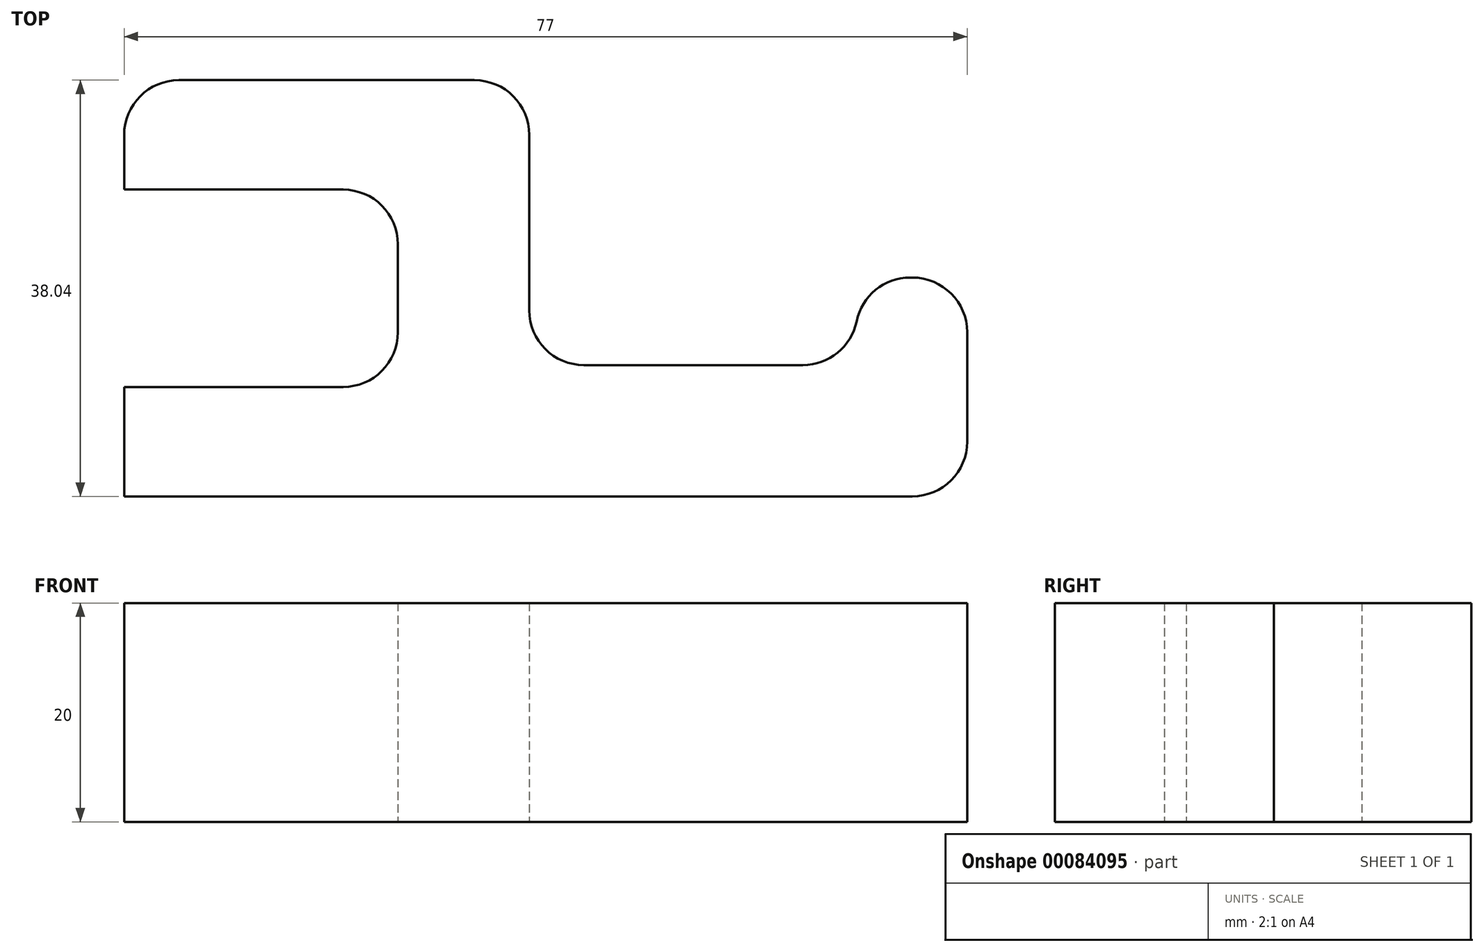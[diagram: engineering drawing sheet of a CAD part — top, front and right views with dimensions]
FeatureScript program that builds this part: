
annotation { "Feature Type Name" : "Feature", "Feature Type Description" : "" }
export const myFeature = defineFeature(function(context is Context, id is Id, definition is map)
    precondition{}
    {
        {
            var Q0;
            Q0=qCreatedBy(makeId("Front.planeOp"),FACE);
            var sketch = newSketch(context, id + "F0", { "sketchPlane" : qUnion([Q0])});
            skLineSegment(sketch, "E0", {"start": v(5, 38.04) * mm, "end": v(32, 38.04) * mm});
            skLineSegment(sketch, "E1", {"start": v(37, 33.04) * mm, "end": v(37, 17) * mm});
            skLineSegment(sketch, "E2", {"start": v(42, 12) * mm, "end": v(62, 12) * mm});
            skLineSegment(sketch, "E3", {"start": v(67, 17) * mm, "end": v(67, 20) * mm});
            skLineSegment(sketch, "E4", {"start": v(67, 20) * mm, "end": v(77, 20) * mm});
            skLineSegment(sketch, "E5", {"start": v(77, 20) * mm, "end": v(77, 5) * mm});
            skLineSegment(sketch, "E6", {"start": v(72, 0) * mm, "end": v(0, 0) * mm});
            skPoint(sketch, "E7.visualSharp", {"position": v(37, 12) * mm});
            skArc(sketch, "E7.filletArc", {"start": v(37, 17) * mm, "mid": v(38.46, 13.46) * mm, "end": v(42, 12) * mm});
            skPoint(sketch, "E8.visualSharp", {"position": v(67, 12) * mm});
            skArc(sketch, "E8.filletArc", {"start": v(62, 12) * mm, "mid": v(65.54, 13.46) * mm, "end": v(67, 17) * mm});
            skPoint(sketch, "E9.visualSharp", {"position": v(77, 0) * mm});
            skArc(sketch, "E9.filletArc", {"start": v(72, 0) * mm, "mid": v(75.54, 1.46) * mm, "end": v(77, 5) * mm});
            skLineSegment(sketch, "E10", {"start": v(0, 28.04) * mm, "end": v(20, 28.04) * mm});
            skLineSegment(sketch, "E11", {"start": v(25, 23.04) * mm, "end": v(25, 15) * mm});
            skLineSegment(sketch, "E12", {"start": v(20, 10) * mm, "end": v(0, 10) * mm});
            skLineSegment(sketch, "E13", {"start": v(0, 10) * mm, "end": v(0, 0) * mm});
            skPoint(sketch, "E14.visualSharp", {"position": v(25, 10) * mm});
            skArc(sketch, "E14.filletArc", {"start": v(20, 10) * mm, "mid": v(23.54, 11.46) * mm, "end": v(25, 15) * mm});
            skPoint(sketch, "E15.visualSharp", {"position": v(25, 28.04) * mm});
            skArc(sketch, "E15.filletArc", {"start": v(25, 23.04) * mm, "mid": v(23.54, 26.58) * mm, "end": v(20, 28.04) * mm});
            skPoint(sketch, "E16.visualSharp", {"position": v(37, 38.04) * mm});
            skArc(sketch, "E16.filletArc", {"start": v(37, 33.04) * mm, "mid": v(35.54, 36.58) * mm, "end": v(32, 38.04) * mm});
            skPoint(sketch, "E17.visualSharp", {"position": v(0, 28.04) * mm});
            skPoint(sketch, "E18.visualSharp", {"position": v(0, 38.04) * mm});
            skArc(sketch, "E18.filletArc", {"start": v(5, 38.04) * mm, "mid": v(1.46, 36.58) * mm, "end": v(0, 33.04) * mm});
            skLineSegment(sketch, "E19", {"start": v(0, 33.04) * mm, "end": v(0, 28.04) * mm});
            skSolve(sketch);
        }
        {
            var Q0;
            Q0 = qSketchRegion(id + "F0", true);
            extrude(context, id + "F1", {"entities" : qUnion([Q0]), "depth" : 20 * mm, "offsetDistance" : 25 * mm});
        }
        {
            var Q0;
            Q0=makeQuery(id+"F1.opExtrude","SWEPT_EDGE",EDGE,{"disambiguationData":[OSD([sQuery(id+"F0.wireOp",EDGE,"E3"),sQuery(id+"F0.wireOp",EDGE,"E4")])]});
            fillet(context, id + "F2", {"entities" : qUnion([Q0]), "radius" : 5 * mm, "tangentPropagation" : true, "allowEdgeOverflow" : false});
        }
        {
            var Q0;
            Q0=makeQuery(id+"F1.opExtrude","SWEPT_EDGE",EDGE,{"disambiguationData":[OSD([sQuery(id+"F0.wireOp",EDGE,"E4"),sQuery(id+"F0.wireOp",EDGE,"E5")])]});
            fillet(context, id + "F3", {"entities" : qUnion([Q0]), "radius" : 5 * mm, "tangentPropagation" : true, "allowEdgeOverflow" : false});
        }
        {
            var Q0;
            Q0=makeQuery(id+"F1.opExtrude","SWEPT_BODY",BODY,{"disambiguationData":[OSD([sQuery(id+"F0.wireOp",EDGE,"E0"),sQuery(id+"F0.wireOp",EDGE,"E1"),sQuery(id+"F0.wireOp",EDGE,"E2"),sQuery(id+"F0.wireOp",EDGE,"E3"),sQuery(id+"F0.wireOp",EDGE,"E4"),sQuery(id+"F0.wireOp",EDGE,"E5"),sQuery(id+"F0.wireOp",EDGE,"E6"),sQuery(id+"F0.wireOp",EDGE,"E7.filletArc"),sQuery(id+"F0.wireOp",EDGE,"E8.filletArc"),sQuery(id+"F0.wireOp",EDGE,"E9.filletArc"),sQuery(id+"F0.wireOp",EDGE,"E10"),sQuery(id+"F0.wireOp",EDGE,"E11"),sQuery(id+"F0.wireOp",EDGE,"E12"),sQuery(id+"F0.wireOp",EDGE,"E13"),sQuery(id+"F0.wireOp",EDGE,"E14.filletArc"),sQuery(id+"F0.wireOp",EDGE,"E15.filletArc"),sQuery(id+"F0.wireOp",EDGE,"E16.filletArc"),sQuery(id+"F0.wireOp",EDGE,"E18.filletArc"),sQuery(id+"F0.wireOp",EDGE,"E19")])]});
            var Q1;
            Q1=makeQuery(id+"F1.opExtrude","CAP_EDGE",EDGE,{"disambiguationData":[OSD([sQuery(id+"F0.wireOp",EDGE,"E6")])],"isStart":true});
            var Q2;
            Q2=makeQuery(id+"F1.opExtrude","CAP_EDGE",EDGE,{"disambiguationData":[OSD([sQuery(id+"F0.wireOp",EDGE,"E6")])],"isStart":true});
            transform(context, id + "F4", {"entities" : qUnion([Q0]), "transformType" : TransformType.ROTATION, "transformAxis" : qUnion([Q2]), "angle" : 90 * degree, "makeCopy" : false});
        }
    });
